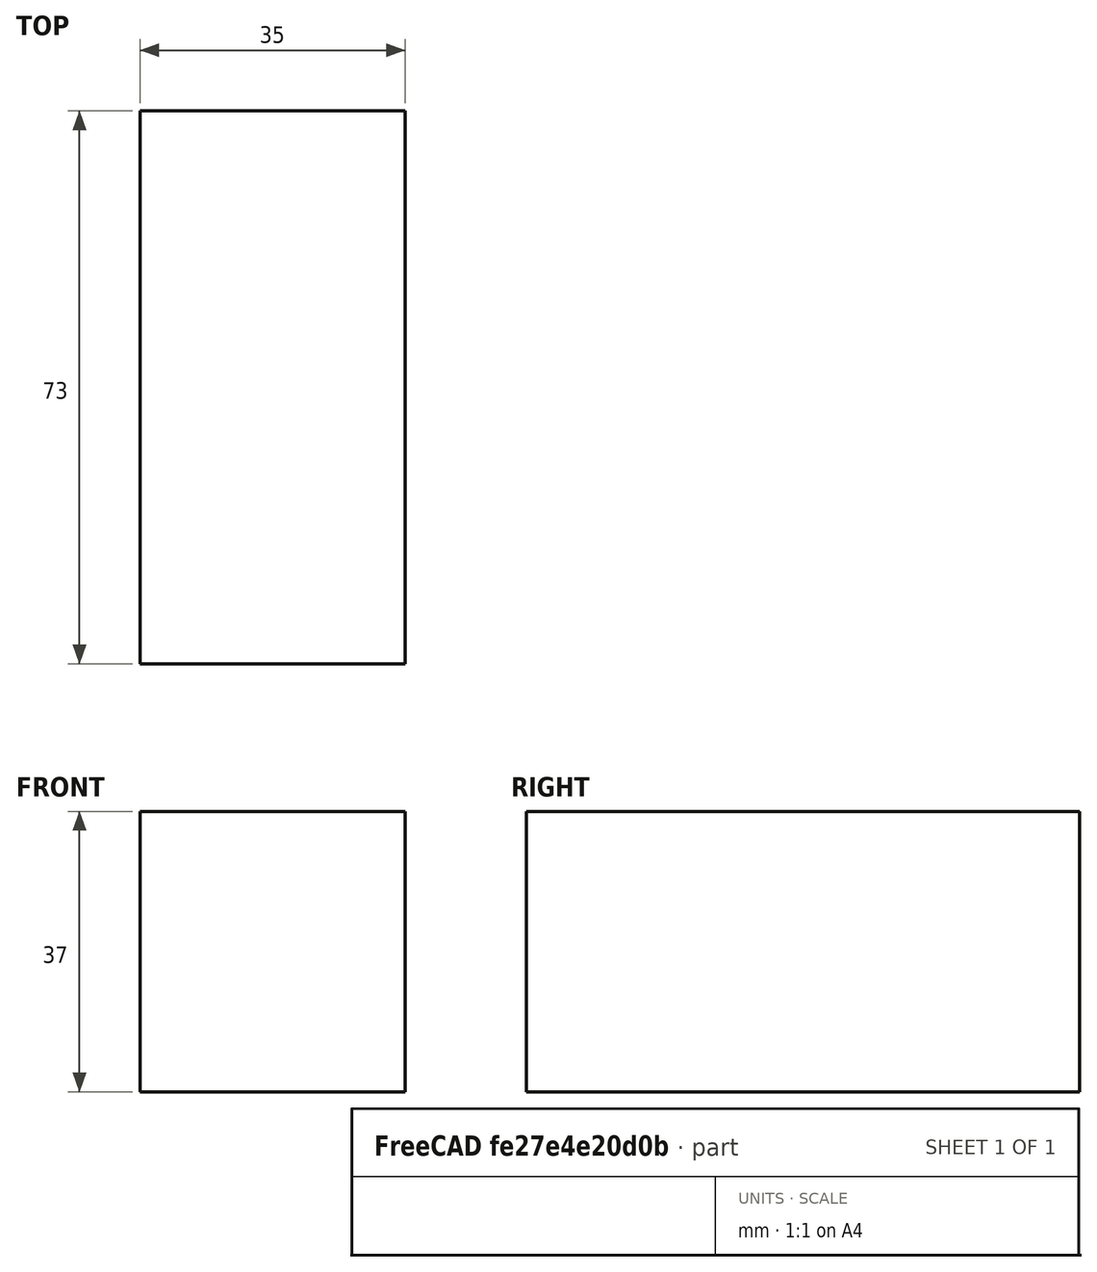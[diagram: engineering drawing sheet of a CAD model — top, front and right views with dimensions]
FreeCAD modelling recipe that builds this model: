
FCSTD DOCUMENT  (FreeCAD 0.18R13638 (Git))
Label: battery_tattu_rline_1550mah
License: All rights reserved
LicenseURL: http://en.wikipedia.org/wiki/All_rights_reserved
objects: Sketcher::SketchObject×1, PartDesign::Pad×1, PartDesign::Body×1
note: 4 computed .brp shape members not serialized (recipe doc carries the construction recipe); baked Part::Feature solids carry a one-line shape summary decoded from their .brp

FEATURE [Sketcher::SketchObject] Sketch
  MapMode = 5
  Support = -> [XY_Plane]
  sketch-geometry (4):
    g0: LineSegment StartX=-17.5 StartY=36.5 StartZ=0 EndX=17.5 EndY=36.5 EndZ=0
    g1: LineSegment StartX=17.5 StartY=36.5 StartZ=0 EndX=17.5 EndY=-36.5 EndZ=0
    g2: LineSegment StartX=17.5 StartY=-36.5 StartZ=0 EndX=-17.5 EndY=-36.5 EndZ=0
    g3: LineSegment StartX=-17.5 StartY=-36.5 StartZ=0 EndX=-17.5 EndY=36.5 EndZ=0
  constraints (12):
    c: Coincident(g0,g1)
    c: Coincident(g1,g2)
    c: Coincident(g2,g3)
    c: Coincident(g3,g0)
    c: Horizontal(g0)
    c: Horizontal(g2)
    c: Vertical(g1)
    c: Vertical(g3)
    c: Symmetric(g0,g0,g-2)
    c: Symmetric(g0,g2,g-1)
    c: DistanceX(g0,g0) = 35
    c: DistanceY(g1,g1) = 73
FEATURE [PartDesign::Pad] Pad
  Length = 37
  Length2 = 100
  Profile = -> Sketch
  Type = 0
FEATURE [PartDesign::Body] Body
  Group = -> [Sketch,Pad]
  Origin = -> Origin
  Tip = -> Pad
